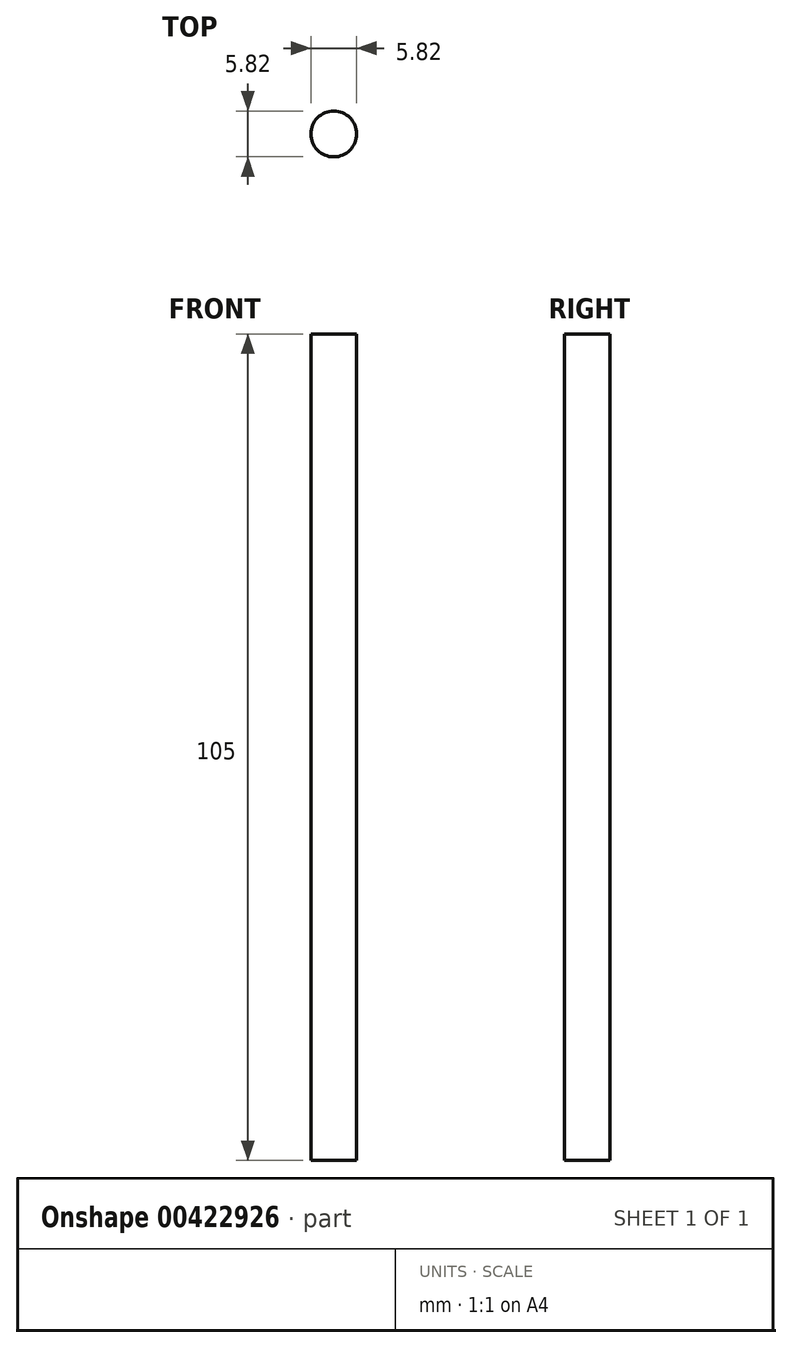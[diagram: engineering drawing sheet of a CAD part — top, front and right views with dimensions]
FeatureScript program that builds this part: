
annotation { "Feature Type Name" : "Feature", "Feature Type Description" : "" }
export const myFeature = defineFeature(function(context is Context, id is Id, definition is map)
    precondition{}
    {
        {
            var Q0;
            Q0=qCreatedBy(makeId("Top.planeOp"),FACE);
            var sketch = newSketch(context, id + "F0", { "sketchPlane" : qUnion([Q0])});
            skCircle(sketch, "E0", {"center": v(0, 0) * mm, "radius": 2.91 * mm});
            skSolve(sketch);
        }
        {
            var Q0;
            Q0=qSketchRegion(id+"F0",true);
            extrude(context, id + "F1", {"entities" : qUnion([Q0]), "depth" : 105 * mm});
        }
    });
